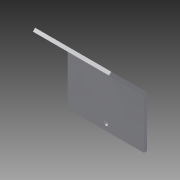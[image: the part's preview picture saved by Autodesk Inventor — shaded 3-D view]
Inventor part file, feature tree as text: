
AUTODESK INVENTOR PART (.ipt)
format: ipt  version: 2015 SP1 (Build 190203100, 203)  size: 115,712 bytes
history: native  units: in
note: dims shown in document units (in); Inventor stores cm internally (conversion verified against a paired STEP export)
features: sketch x3, hole x2, projected_geometry x2, extrude x1
ambient origin geometry x8: Origin, YZ Plane, XZ Plane, XY Plane, X Axis, Y Axis, Z Axis, Center Point
bodies: Solid1 (feature_tree)
feature tree (8):
  extrude  "Extrusion1"  Depth=0.125in
  hole  "Hole1"  [1 undecoded]
  hole  "Hole2"  [1 undecoded]
  sketch  "Sketch1"  dims[d0=2.0in d1=0.125in]
  sketch  "Sketch2"  dims[d2=2.0in d3=45.0deg]
  projected_geometry  "Projected Loop1"
  sketch  "Sketch3"  dims[d4=0.125in d5=3.0in d6=0.0in d7=1.5in d8=1.5in d9=0.5in d10=0.5in d11=0.25in d12=0.75in d13=0.375in d14=0.25in d15=0.5635in d16=1.0in d17=0.8108in d18=0.25in d19=1.5in d20=0.1562in d21=0.75in d22=0.375in d23=0.25in d24=0.5635in d25=1.0in d26=0.8108in]
  projected_geometry  "Projected Loop2"
note: 2 required parameter values undecoded (feature->parameter linkage not recoverable at this tier; creation-order binding heuristic only, values carry confidence <= 0.55)
